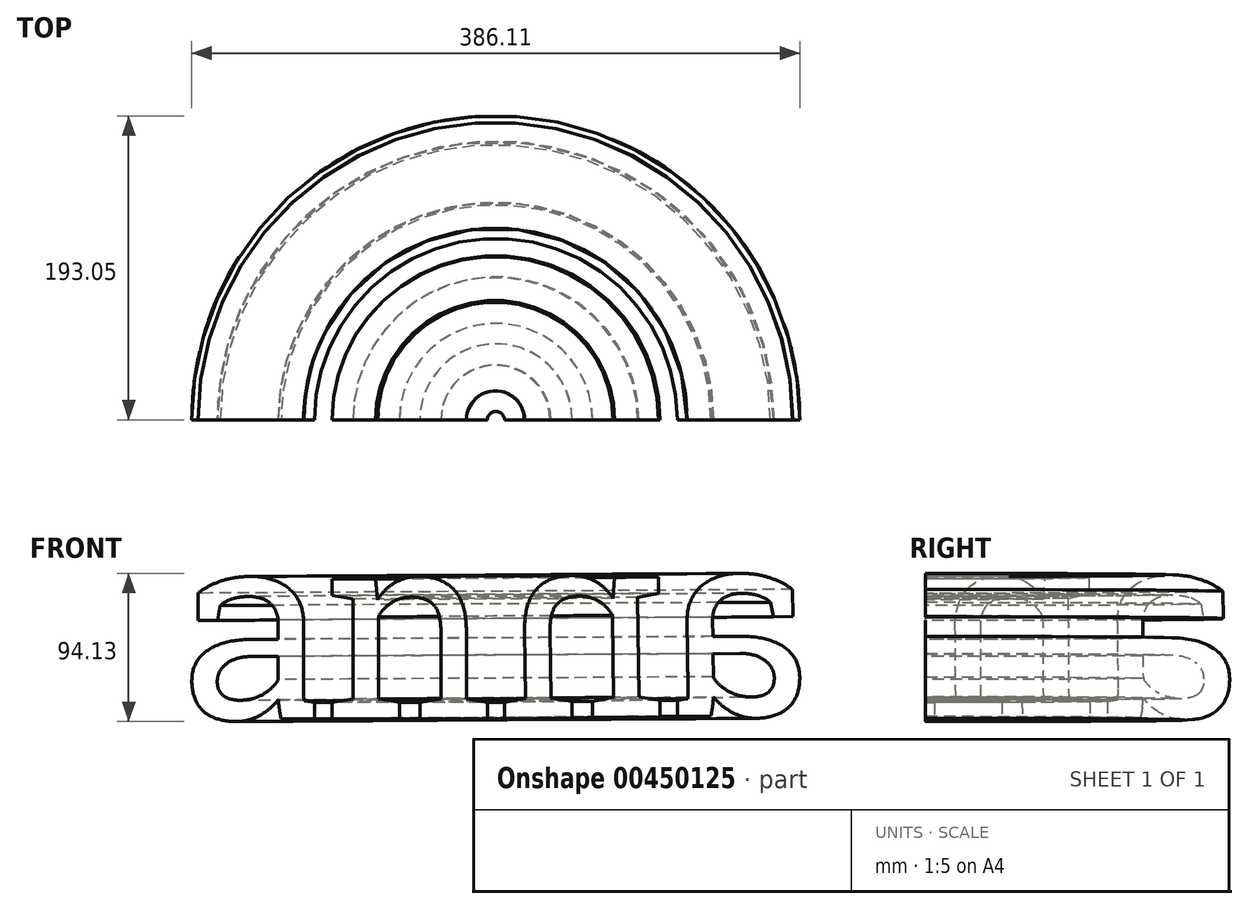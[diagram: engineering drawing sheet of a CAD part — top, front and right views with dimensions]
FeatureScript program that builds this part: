
annotation { "Feature Type Name" : "Feature", "Feature Type Description" : "" }
export const myFeature = defineFeature(function(context is Context, id is Id, definition is map)
    precondition{}
    {
        {
            var Q0;
            Q0=qCreatedBy(makeId("Front.planeOp"),FACE);
            var sketch = newSketch(context, id + "F0", { "sketchPlane" : qUnion([Q0])});
            skText(sketch, "E0", { "text": "an", "fontName": "RobotoSlab-Regular.ttf"});
            const initialGuessF0  = {"E0": [-0.06833, -0.05302, 1, 0, 0.12099]};
            skSetInitialGuess(sketch, initialGuessF0);
            skSolve(sketch);
        }
        {
            var Q0;
            Q0=makeQuery(id+"F0.imprint","IMPRINT",FACE,{"disambiguationData":[TD([[makeQuery(id+"F0.imprint","IMPRINT",EDGE,{"derivedFrom":sQuery(id+"F0.wireOp",EDGE,"E0.sketch_text.stroke-0")}),-1.0]])]});
            var sketch = newSketch(context, id + "F1", { "sketchPlane" : qUnion([Q0])});
            skLineSegment(sketch, "E1", {"start": v(133.41, -53.03) * mm, "end": v(132.58, 79.03) * mm});
            skLineSegment(sketch, "E2", {"start": v(132.58, 79.03) * mm, "end": v(133.41, -53.03) * mm});
            skSolve(sketch);
        }
        {
            var Q0;
            Q0=makeQuery(id+"F0.imprint","IMPRINT",FACE,{"disambiguationData":[TD([[makeQuery(id+"F0.imprint","IMPRINT",EDGE,{"derivedFrom":sQuery(id+"F0.wireOp",EDGE,"E0.sketch_text.stroke-35")}),-1.0]])]});
            var Q1;
            Q1=makeQuery(id+"F1.imprint","IMPRINT",FACE,{"disambiguationData":[TD([[makeQuery(id+"F1.imprint","IMPRINT",EDGE,{"derivedFrom":makeQuery(id+"F0.imprint","IMPRINT",EDGE,{"derivedFrom":sQuery(id+"F0.wireOp",EDGE,"E0.sketch_text.stroke-0")})}),-1.0]])]});
            var Q2;
            Q2=sQuery(id+"F1.wireOp",EDGE,"E2");
            revolve(context, id + "F2", {"entities" : qUnion([Q0, Q1]), "axis" : qUnion([Q2]), "revolveType" : RevolveType.ONE_DIRECTION, "angle" : 180 * degree});
        }
    });
